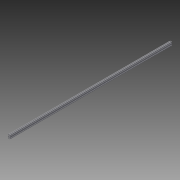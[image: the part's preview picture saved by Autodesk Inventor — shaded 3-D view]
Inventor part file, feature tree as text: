
AUTODESK INVENTOR PART (.ipt)
format: ipt  version: 2013 (Build 170138000, 138)  size: 267,264 bytes
history: native  units: in
note: dims shown in document units (in); Inventor stores cm internally (conversion verified against a paired STEP export)
features: extrude x1, sketch x1
ambient origin geometry x8: Origin, YZ Plane, XZ Plane, XY Plane, X Axis, Y Axis, Z Axis, Center Point
bodies: Solid1 (feature_tree)
feature tree (2):
  extrude  "Extrusion1"  [1 undecoded]
  sketch  "Sketch1"  dims[d0=70.8661in d1=0.0in]
note: 1 required parameter value undecoded (feature->parameter linkage not recoverable at this tier; creation-order binding heuristic only, values carry confidence <= 0.55)
